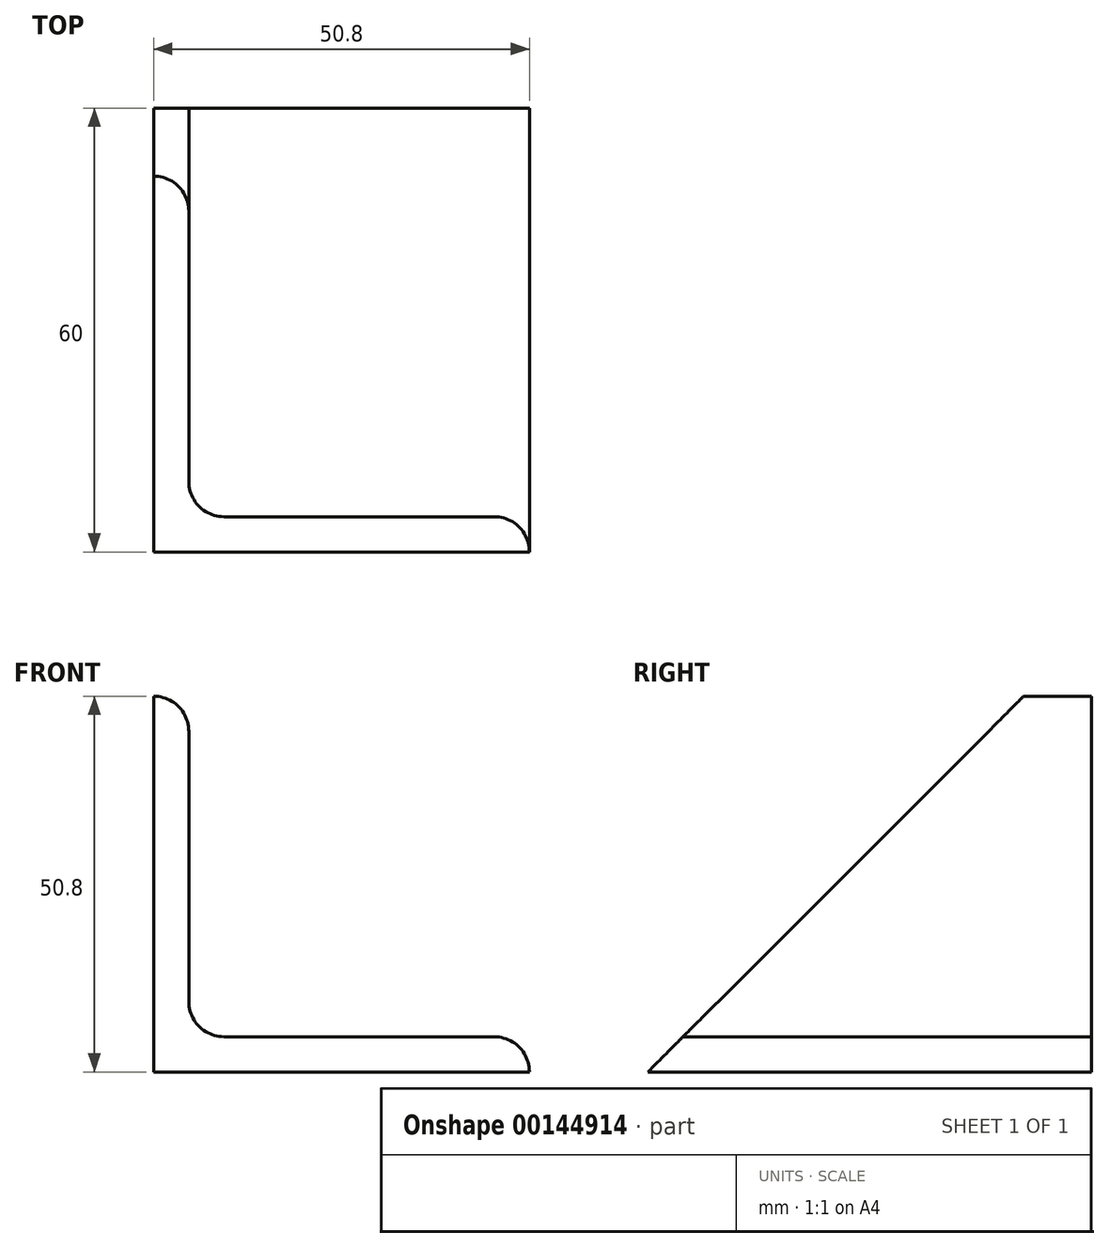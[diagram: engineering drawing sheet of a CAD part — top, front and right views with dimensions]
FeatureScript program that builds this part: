
annotation { "Feature Type Name" : "Feature", "Feature Type Description" : "" }
export const myFeature = defineFeature(function(context is Context, id is Id, definition is map)
    precondition{}
    {
        {
            assignVariable(context, id + "F0", {"name" : "AngleLength", "anyValue" : 60});
        }
        {
            var Q0;
            Q0=qCreatedBy(makeId("Front.planeOp"),FACE);
            var sketch = newSketch(context, id + "F1", { "sketchPlane" : qUnion([Q0])});
            skLineSegment(sketch, "E0", {"start": v(0, 0) * mm, "end": v(0, -50.8) * mm});
            skLineSegment(sketch, "E1", {"start": v(0, -50.8) * mm, "end": v(50.8, -50.8) * mm});
            skLineSegment(sketch, "E2", {"start": v(50.8, -50.8) * mm, "end": v(50.8, -50.8) * mm});
            skLineSegment(sketch, "E3", {"start": v(46.04, -46.04) * mm, "end": v(9.53, -46.04) * mm});
            skLineSegment(sketch, "E4", {"start": v(4.76, -41.27) * mm, "end": v(4.76, -4.76) * mm});
            skLineSegment(sketch, "E5", {"start": v(0, 0) * mm, "end": v(0, 0) * mm});
            skPoint(sketch, "E6.visualSharp", {"position": v(4.76, -46.04) * mm});
            skArc(sketch, "E6.filletArc", {"start": v(4.76, -41.27) * mm, "mid": v(6.16, -44.64) * mm, "end": v(9.53, -46.04) * mm});
            skPoint(sketch, "E7.visualSharp", {"position": v(4.76, 0) * mm});
            skArc(sketch, "E7.filletArc", {"start": v(4.76, -4.76) * mm, "mid": v(3.37, -1.4) * mm, "end": v(0, 0) * mm});
            skPoint(sketch, "E8.visualSharp", {"position": v(50.8, -46.04) * mm});
            skArc(sketch, "E8.filletArc", {"start": v(50.8, -50.8) * mm, "mid": v(49.4, -47.43) * mm, "end": v(46.04, -46.04) * mm});
            skSolve(sketch);
        }
        {
            var Q0;
            Q0=makeQuery(id+"F1.imprint","IMPRINT",FACE,{"disambiguationData":[TD([[makeQuery(id+"F1.imprint","IMPRINT",EDGE,{"derivedFrom":sQuery(id+"F1.wireOp",EDGE,"E0")}),1.0]])]});
            extrude(context, id + "F2", {"entities" : qUnion([Q0]), "oppositeDirection" : true, "depth" : (getVariable(context, 'AngleLength')) * mm});
        }
        {
            var Q0;
            Q0=makeQuery(id+"F2.opExtrude","SWEPT_FACE",FACE,{"disambiguationData":[OSD([sQuery(id+"F1.wireOp",EDGE,"E0")])]});
            var sketch = newSketch(context, id + "F3", { "sketchPlane" : qUnion([Q0])});
            skLineSegment(sketch, "E9", {"start": v(0, -50.8) * mm, "end": v(-50.8, 0) * mm});
            skLineSegment(sketch, "E10", {"start": v(-50.8, 0) * mm, "end": v(0, 0) * mm});
            skLineSegment(sketch, "E11", {"start": v(0, 0) * mm, "end": v(0, -50.8) * mm});
            skLineSegment(sketch, "E12", {"start": v(-1524, -50.8) * mm, "end": v(-1473.2, 0) * mm});
            skLineSegment(sketch, "E13", {"start": v(-1473.2, 0) * mm, "end": v(-1524, 0) * mm});
            skLineSegment(sketch, "E14", {"start": v(-1524, 0) * mm, "end": v(-1524, -50.8) * mm});
            skSolve(sketch);
        }
        {
            var Q0;
            Q0=qSketchRegion(id+"F3",true);
            extrude(context, id + "F4", {"entities" : qUnion([Q0]), "operationType" : NewBodyOperationType.REMOVE, "oppositeDirection" : true, "depth" : 50.8 * mm});
        }
    });
